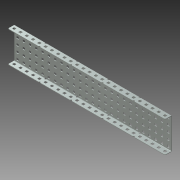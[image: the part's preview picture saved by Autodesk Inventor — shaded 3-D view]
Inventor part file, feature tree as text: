
AUTODESK INVENTOR PART (.ipt)
format: ipt  version: 2015 (Build 190159000, 159)  size: 3,633,664 bytes
history: native  units: mm (DEFAULTED — no unit token found)
features: other x175, extrude x175, pattern_linear x2, sketch x2, imported_body x1, plane x1, mirror x1
ambient origin geometry x8: Origin, YZ Plane, XZ Plane, XY Plane, X Axis, Y Axis, Z Axis, Center Point
bodies: Solid1 (feature_tree)
feature tree (357):
  imported_body  "Base1"
  pattern_linear  "Rectangular Pattern1"  Count1=25  [1 undecoded]
  pattern_linear  "Rectangular Pattern2"  Spacing1=12.7mm  [1 undecoded]
  plane  "Work Plane1"
  mirror  "Mirror1"
  sketch  "Sketch1"  dims[d1=1.1684mm]
  other  "Srf1"
  other  "Srf2"
  other  "Srf3"
  other  "Srf4"
  other  "Srf5"
  other  "Srf6"
  other  "Srf7"
  other  "Srf8"
  other  "Srf9"
  other  "Srf10"
  other  "Srf11"
  other  "Srf12"
  other  "Srf13"
  other  "Srf14"
  other  "Srf15"
  other  "Srf16"
  other  "Srf17"
  other  "Srf18"
  other  "Srf19"
  other  "Srf20"
  other  "Srf21"
  other  "Srf22"
  other  "Srf23"
  other  "Srf24"
  other  "Srf25"
  other  "Srf26"
  other  "Srf27"
  other  "Srf28"
  other  "Srf29"
  other  "Srf30"
  other  "Srf31"
  other  "Srf32"
  other  "Srf33"
  other  "Srf34"
  other  "Srf35"
  other  "Srf36"
  other  "Srf37"
  other  "Srf38"
  other  "Srf39"
  other  "Srf40"
  other  "Srf41"
  other  "Srf42"
  other  "Srf43"
  other  "Srf44"
  other  "Srf45"
  other  "Srf46"
  other  "Srf47"
  other  "Srf48"
  other  "Srf49"
  other  "Srf50"
  other  "Srf51"
  other  "Srf52"
  other  "Srf53"
  other  "Srf54"
  other  "Srf55"
  other  "Srf56"
  other  "Srf57"
  other  "Srf58"
  other  "Srf59"
  other  "Srf60"
  other  "Srf61"
  other  "Srf62"
  other  "Srf63"
  other  "Srf64"
  other  "Srf65"
  other  "Srf66"
  other  "Srf67"
  other  "Srf68"
  other  "Srf69"
  other  "Srf70"
  other  "Srf71"
  other  "Srf72"
  other  "Srf73"
  other  "Srf74"
  other  "Srf75"
  other  "Srf76"
  other  "Srf77"
  other  "Srf78"
  other  "Srf79"
  other  "Srf80"
  other  "Srf81"
  other  "Srf82"
  other  "Srf83"
  other  "Srf84"
  other  "Srf85"
  other  "Srf86"
  other  "Srf87"
  other  "Srf88"
  other  "Srf89"
  other  "Srf90"
  other  "Srf91"
  other  "Srf92"
  other  "Srf93"
  other  "Srf94"
  other  "Srf95"
  other  "Srf96"
  other  "Srf97"
  other  "Srf98"
  other  "Srf99"
  other  "Srf100"
  other  "Srf101"
  other  "Srf102"
  other  "Srf103"
  other  "Srf104"
  other  "Srf105"
  other  "Srf106"
  other  "Srf107"
  other  "Srf108"
  other  "Srf109"
  other  "Srf110"
  other  "Srf111"
  other  "Srf112"
  other  "Srf113"
  other  "Srf114"
  other  "Srf115"
  other  "Srf116"
  other  "Srf117"
  other  "Srf118"
  other  "Srf119"
  other  "Srf120"
  other  "Srf121"
  other  "Srf122"
  other  "Srf123"
  other  "Srf124"
  other  "Srf125"
  sketch  "Sketch2"  dims[d2=0.0mm d3=250.0mm d5=12.7mm d6=50.0mm d8=12.7mm d9=1.1684mm d10=0.0mm d11=250.0mm d13=12.7mm d14=0.0mm d15=0.0mm d16=0.0mm d17=0.0mm d18=0.0mm d19=0.0mm d20=0.0mm d21=0.0mm d22=0.0mm d23=0.0mm d24=0.0mm d25=0.0mm d26=0.0mm d27=0.0mm d28=0.0mm d29=0.0mm d30=0.0mm d31=0.0mm d32=0.0mm d33=0.0mm d34=0.0mm d35=0.0mm d36=0.0mm d37=0.0mm d38=0.0mm d39=0.0mm d40=0.0mm d41=0.0mm d42=0.0mm d43=0.0mm d44=0.0mm d45=0.0mm d46=0.0mm d47=0.0mm d48=0.0mm d49=0.0mm d50=0.0mm d51=0.0mm d52=0.0mm d53=0.0mm d54=0.0mm d55=0.0mm d56=0.0mm d57=0.0mm d58=0.0mm d59=0.0mm d60=0.0mm d61=0.0mm d62=0.0mm d63=0.0mm d64=0.0mm d65=0.0mm d66=0.0mm d67=0.0mm d68=0.0mm d69=0.0mm d70=0.0mm d71=0.0mm d72=0.0mm d73=0.0mm d74=0.0mm d75=0.0mm d76=0.0mm d77=0.0mm d78=0.0mm d79=0.0mm d80=0.0mm d81=0.0mm d82=0.0mm d83=0.0mm d84=0.0mm d85=0.0mm d86=0.0mm d87=0.0mm d88=0.0mm d89=0.0mm d90=0.0mm d91=0.0mm d92=0.0mm d93=0.0mm d94=0.0mm d95=0.0mm d96=0.0mm d97=0.0mm d98=0.0mm d99=0.0mm d100=0.0mm d101=0.0mm d102=0.0mm d103=0.0mm d104=0.0mm d105=0.0mm d106=0.0mm d107=0.0mm d108=0.0mm d109=0.0mm d110=0.0mm d111=0.0mm d112=0.0mm d113=0.0mm d114=0.0mm d115=0.0mm d116=0.0mm d117=0.0mm d118=0.0mm d119=0.0mm d120=0.0mm d121=0.0mm d122=0.0mm d123=0.0mm d124=0.0mm d125=0.0mm d126=0.0mm d127=0.0mm d128=0.0mm d129=0.0mm d130=0.0mm d131=0.0mm d132=0.0mm d133=0.0mm d134=0.0mm d135=0.0mm d136=0.0mm d137=0.0mm d138=0.0mm d139=0.0mm d140=0.0mm d141=0.0mm d142=0.0mm d143=0.0mm d144=0.0mm d145=0.0mm d146=0.0mm d147=0.0mm d148=0.0mm d149=0.0mm d150=0.0mm d151=0.0mm d152=0.0mm d153=0.0mm d154=0.0mm d155=0.0mm d156=0.0mm d157=0.0mm d158=0.0mm d159=0.0mm d160=0.0mm d161=0.0mm d162=0.0mm d163=0.0mm d164=0.0mm d165=0.0mm d166=0.0mm d167=0.0mm d168=0.0mm d169=0.0mm d170=0.0mm d171=0.0mm d172=0.0mm d173=0.0mm d174=0.0mm d175=0.0mm d176=0.0mm d177=0.0mm d178=0.0mm d179=0.0mm d180=0.0mm d181=0.0mm d182=0.0mm d183=0.0mm d184=0.0mm d185=0.0mm d186=0.0mm d187=0.0mm d188=0.0mm d189=0.0mm d190=0.0mm d191=0.0mm d192=0.0mm d193=0.0mm d194=0.0mm d195=0.0mm d196=0.0mm d197=0.0mm d198=0.0mm d199=0.0mm d200=0.0mm d201=0.0mm d202=0.0mm d203=0.0mm d204=0.0mm d205=0.0mm d206=0.0mm d207=0.0mm d208=0.0mm d209=0.0mm d210=0.0mm d211=0.0mm d212=0.0mm d213=0.0mm d214=0.0mm d215=0.0mm d216=0.0mm d217=0.0mm d218=0.0mm d219=0.0mm d220=0.0mm d221=0.0mm d222=0.0mm d223=0.0mm d224=0.0mm d225=0.0mm d226=0.0mm d227=0.0mm d228=0.0mm d229=0.0mm d230=0.0mm d231=0.0mm d232=0.0mm d233=0.0mm d234=0.0mm d235=0.0mm d236=0.0mm d237=0.0mm d238=0.0mm d239=0.0mm d240=0.0mm d241=0.0mm d242=0.0mm d243=0.0mm d244=0.0mm d245=0.0mm d246=0.0mm d247=0.0mm d248=0.0mm d249=0.0mm d250=0.0mm d251=0.0mm d252=0.0mm d253=0.0mm d254=0.0mm d255=0.0mm d256=0.0mm d257=0.0mm d258=0.0mm d259=0.0mm d260=0.0mm d261=0.0mm d262=0.0mm d263=0.0mm d264=0.0mm d265=0.0mm d266=0.0mm d267=0.0mm d268=0.0mm d269=0.0mm d270=0.0mm d271=0.0mm d272=0.0mm d273=0.0mm d274=0.0mm d275=0.0mm d276=0.0mm d277=0.0mm d278=0.0mm d279=0.0mm d280=0.0mm d281=0.0mm d282=0.0mm d283=0.0mm d284=0.0mm d285=0.0mm d286=0.0mm d287=0.0mm d288=0.0mm d289=0.0mm d290=0.0mm d291=0.0mm d292=0.0mm d293=0.0mm d294=0.0mm d295=0.0mm d296=0.0mm d297=0.0mm d298=0.0mm d299=0.0mm d300=0.0mm d301=0.0mm d302=0.0mm d303=0.0mm d304=0.0mm d305=0.0mm d306=0.0mm d307=0.0mm d308=0.0mm d309=0.0mm d310=0.0mm d311=0.0mm d312=0.0mm d313=0.0mm d314=0.0mm d315=0.0mm d316=0.0mm d317=0.0mm d318=0.0mm d319=0.0mm d320=0.0mm d321=0.0mm d322=0.0mm d323=0.0mm d324=0.0mm d325=0.0mm d326=0.0mm d327=0.0mm d328=0.0mm d329=0.0mm d330=0.0mm d331=0.0mm d332=0.0mm d333=0.0mm d334=0.0mm d335=0.0mm d336=0.0mm d337=0.0mm d338=0.0mm d339=0.0mm d340=0.0mm d341=0.0mm d342=0.0mm d343=0.0mm d344=0.0mm d345=0.0mm d346=0.0mm d347=0.0mm d348=0.0mm d349=0.0mm d350=0.0mm d351=0.0mm d352=0.0mm d353=0.0mm d354=0.0mm d355=0.0mm d356=0.0mm d357=0.0mm d358=0.0mm d359=0.0mm d360=0.0mm d361=0.0mm d362=0.0mm d363=0.0mm]
  other  "Srf126"
  other  "Srf127"
  other  "Srf128"
  other  "Srf129"
  other  "Srf130"
  other  "Srf131"
  other  "Srf132"
  other  "Srf133"
  other  "Srf134"
  other  "Srf135"
  other  "Srf136"
  other  "Srf137"
  other  "Srf138"
  other  "Srf139"
  other  "Srf140"
  other  "Srf141"
  other  "Srf142"
  other  "Srf143"
  other  "Srf144"
  other  "Srf145"
  other  "Srf146"
  other  "Srf147"
  other  "Srf148"
  other  "Srf149"
  other  "Srf150"
  other  "Srf175"
  other  "Srf151"
  other  "Srf152"
  other  "Srf153"
  other  "Srf154"
  other  "Srf155"
  other  "Srf156"
  other  "Srf157"
  other  "Srf158"
  other  "Srf159"
  other  "Srf160"
  other  "Srf161"
  other  "Srf162"
  other  "Srf163"
  other  "Srf164"
  other  "Srf165"
  other  "Srf166"
  other  "Srf167"
  other  "Srf168"
  other  "Srf169"
  other  "Srf170"
  other  "Srf171"
  other  "Srf172"
  other  "Srf173"
  other  "Srf174"
  extrude  "ExtrusionSrf1"  Depth=50.0mm
  extrude  "ExtrusionSrf126"  Depth=1.1684mm
  extrude  "ExtrusionSrf2"  TaperAngle=0.0deg  [1 undecoded]
  extrude  "ExtrusionSrf3"  Depth=250.0mm
  extrude  "ExtrusionSrf4"  Depth=12.7mm
  extrude  "ExtrusionSrf5"  TaperAngle=0.0deg  [1 undecoded]
  extrude  "ExtrusionSrf6"  TaperAngle=0.0deg  [1 undecoded]
  extrude  "ExtrusionSrf7"  TaperAngle=0.0deg  [1 undecoded]
  extrude  "ExtrusionSrf8"  TaperAngle=0.0deg  [1 undecoded]
  extrude  "ExtrusionSrf9"  TaperAngle=0.0deg  [1 undecoded]
  extrude  "ExtrusionSrf10"  TaperAngle=0.0deg  [1 undecoded]
  extrude  "ExtrusionSrf11"  TaperAngle=0.0deg  [1 undecoded]
  extrude  "ExtrusionSrf12"  TaperAngle=0.0deg  [1 undecoded]
  extrude  "ExtrusionSrf13"  TaperAngle=0.0deg  [1 undecoded]
  extrude  "ExtrusionSrf14"  TaperAngle=0.0deg  [1 undecoded]
  extrude  "ExtrusionSrf15"  TaperAngle=0.0deg  [1 undecoded]
  extrude  "ExtrusionSrf16"  TaperAngle=0.0deg  [1 undecoded]
  extrude  "ExtrusionSrf17"  TaperAngle=0.0deg  [1 undecoded]
  extrude  "ExtrusionSrf18"  TaperAngle=0.0deg  [1 undecoded]
  extrude  "ExtrusionSrf19"  TaperAngle=0.0deg  [1 undecoded]
  extrude  "ExtrusionSrf20"  TaperAngle=0.0deg  [1 undecoded]
  extrude  "ExtrusionSrf21"  TaperAngle=0.0deg  [1 undecoded]
  extrude  "ExtrusionSrf22"  TaperAngle=0.0deg  [1 undecoded]
  extrude  "ExtrusionSrf23"  TaperAngle=0.0deg  [1 undecoded]
  extrude  "ExtrusionSrf24"  TaperAngle=0.0deg  [1 undecoded]
  extrude  "ExtrusionSrf25"  TaperAngle=0.0deg  [1 undecoded]
  extrude  "ExtrusionSrf26"  TaperAngle=0.0deg  [1 undecoded]
  extrude  "ExtrusionSrf27"  TaperAngle=0.0deg  [1 undecoded]
  extrude  "ExtrusionSrf28"  TaperAngle=0.0deg  [1 undecoded]
  extrude  "ExtrusionSrf29"  TaperAngle=0.0deg  [1 undecoded]
  extrude  "ExtrusionSrf30"  TaperAngle=0.0deg  [1 undecoded]
  extrude  "ExtrusionSrf31"  TaperAngle=0.0deg  [1 undecoded]
  extrude  "ExtrusionSrf32"  TaperAngle=0.0deg  [1 undecoded]
  extrude  "ExtrusionSrf33"  TaperAngle=0.0deg  [1 undecoded]
  extrude  "ExtrusionSrf34"  TaperAngle=0.0deg  [1 undecoded]
  extrude  "ExtrusionSrf35"  TaperAngle=0.0deg  [1 undecoded]
  extrude  "ExtrusionSrf36"  TaperAngle=0.0deg  [1 undecoded]
  extrude  "ExtrusionSrf37"  TaperAngle=0.0deg  [1 undecoded]
  extrude  "ExtrusionSrf38"  TaperAngle=0.0deg  [1 undecoded]
  extrude  "ExtrusionSrf39"  TaperAngle=0.0deg  [1 undecoded]
  extrude  "ExtrusionSrf40"  TaperAngle=0.0deg  [1 undecoded]
  extrude  "ExtrusionSrf41"  TaperAngle=0.0deg  [1 undecoded]
  extrude  "ExtrusionSrf42"  TaperAngle=0.0deg  [1 undecoded]
  extrude  "ExtrusionSrf43"  TaperAngle=0.0deg  [1 undecoded]
  extrude  "ExtrusionSrf44"  TaperAngle=0.0deg  [1 undecoded]
  extrude  "ExtrusionSrf45"  TaperAngle=0.0deg  [1 undecoded]
  extrude  "ExtrusionSrf46"  TaperAngle=0.0deg  [1 undecoded]
  extrude  "ExtrusionSrf47"  TaperAngle=0.0deg  [1 undecoded]
  extrude  "ExtrusionSrf48"  TaperAngle=0.0deg  [1 undecoded]
  extrude  "ExtrusionSrf49"  TaperAngle=0.0deg  [1 undecoded]
  extrude  "ExtrusionSrf50"  TaperAngle=0.0deg  [1 undecoded]
  extrude  "ExtrusionSrf51"  TaperAngle=0.0deg  [1 undecoded]
  extrude  "ExtrusionSrf52"  TaperAngle=0.0deg  [1 undecoded]
  extrude  "ExtrusionSrf53"  TaperAngle=0.0deg  [1 undecoded]
  extrude  "ExtrusionSrf54"  TaperAngle=0.0deg  [1 undecoded]
  extrude  "ExtrusionSrf55"  TaperAngle=0.0deg  [1 undecoded]
  extrude  "ExtrusionSrf56"  TaperAngle=0.0deg  [1 undecoded]
  extrude  "ExtrusionSrf57"  TaperAngle=0.0deg  [1 undecoded]
  extrude  "ExtrusionSrf58"  TaperAngle=0.0deg  [1 undecoded]
  extrude  "ExtrusionSrf59"  TaperAngle=0.0deg  [1 undecoded]
  extrude  "ExtrusionSrf60"  TaperAngle=0.0deg  [1 undecoded]
  extrude  "ExtrusionSrf61"  TaperAngle=0.0deg  [1 undecoded]
  extrude  "ExtrusionSrf62"  TaperAngle=0.0deg  [1 undecoded]
  extrude  "ExtrusionSrf63"  TaperAngle=0.0deg  [1 undecoded]
  extrude  "ExtrusionSrf64"  TaperAngle=0.0deg  [1 undecoded]
  extrude  "ExtrusionSrf65"  TaperAngle=0.0deg  [1 undecoded]
  extrude  "ExtrusionSrf66"  TaperAngle=0.0deg  [1 undecoded]
  extrude  "ExtrusionSrf67"  TaperAngle=0.0deg  [1 undecoded]
  extrude  "ExtrusionSrf68"  TaperAngle=0.0deg  [1 undecoded]
  extrude  "ExtrusionSrf69"  TaperAngle=0.0deg  [1 undecoded]
  extrude  "ExtrusionSrf70"  TaperAngle=0.0deg  [1 undecoded]
  extrude  "ExtrusionSrf71"  TaperAngle=0.0deg  [1 undecoded]
  extrude  "ExtrusionSrf72"  TaperAngle=0.0deg  [1 undecoded]
  extrude  "ExtrusionSrf73"  TaperAngle=0.0deg  [1 undecoded]
  extrude  "ExtrusionSrf74"  TaperAngle=0.0deg  [1 undecoded]
  extrude  "ExtrusionSrf75"  TaperAngle=0.0deg  [1 undecoded]
  extrude  "ExtrusionSrf76"  TaperAngle=0.0deg  [1 undecoded]
  extrude  "ExtrusionSrf77"  TaperAngle=0.0deg  [1 undecoded]
  extrude  "ExtrusionSrf78"  TaperAngle=0.0deg  [1 undecoded]
  extrude  "ExtrusionSrf79"  TaperAngle=0.0deg  [1 undecoded]
  extrude  "ExtrusionSrf80"  TaperAngle=0.0deg  [1 undecoded]
  extrude  "ExtrusionSrf81"  TaperAngle=0.0deg  [1 undecoded]
  extrude  "ExtrusionSrf82"  TaperAngle=0.0deg  [1 undecoded]
  extrude  "ExtrusionSrf83"  TaperAngle=0.0deg  [1 undecoded]
  extrude  "ExtrusionSrf84"  TaperAngle=0.0deg  [1 undecoded]
  extrude  "ExtrusionSrf85"  TaperAngle=0.0deg  [1 undecoded]
  extrude  "ExtrusionSrf86"  TaperAngle=0.0deg  [1 undecoded]
  extrude  "ExtrusionSrf87"  TaperAngle=0.0deg  [1 undecoded]
  extrude  "ExtrusionSrf88"  TaperAngle=0.0deg  [1 undecoded]
  extrude  "ExtrusionSrf89"  TaperAngle=0.0deg  [1 undecoded]
  extrude  "ExtrusionSrf90"  TaperAngle=0.0deg  [1 undecoded]
  extrude  "ExtrusionSrf91"  TaperAngle=0.0deg  [1 undecoded]
  extrude  "ExtrusionSrf92"  TaperAngle=0.0deg  [1 undecoded]
  extrude  "ExtrusionSrf93"  TaperAngle=0.0deg  [1 undecoded]
  extrude  "ExtrusionSrf94"  TaperAngle=0.0deg  [1 undecoded]
  extrude  "ExtrusionSrf95"  TaperAngle=0.0deg  [1 undecoded]
  extrude  "ExtrusionSrf96"  TaperAngle=0.0deg  [1 undecoded]
  extrude  "ExtrusionSrf97"  TaperAngle=0.0deg  [1 undecoded]
  extrude  "ExtrusionSrf98"  TaperAngle=0.0deg  [1 undecoded]
  extrude  "ExtrusionSrf99"  TaperAngle=0.0deg  [1 undecoded]
  extrude  "ExtrusionSrf100"  TaperAngle=0.0deg  [1 undecoded]
  extrude  "ExtrusionSrf101"  TaperAngle=0.0deg  [1 undecoded]
  extrude  "ExtrusionSrf102"  TaperAngle=0.0deg  [1 undecoded]
  extrude  "ExtrusionSrf103"  TaperAngle=0.0deg  [1 undecoded]
  extrude  "ExtrusionSrf104"  TaperAngle=0.0deg  [1 undecoded]
  extrude  "ExtrusionSrf105"  TaperAngle=0.0deg  [1 undecoded]
  extrude  "ExtrusionSrf106"  TaperAngle=0.0deg  [1 undecoded]
  extrude  "ExtrusionSrf107"  TaperAngle=0.0deg  [1 undecoded]
  extrude  "ExtrusionSrf108"  TaperAngle=0.0deg  [1 undecoded]
  extrude  "ExtrusionSrf109"  TaperAngle=0.0deg  [1 undecoded]
  extrude  "ExtrusionSrf110"  TaperAngle=0.0deg  [1 undecoded]
  extrude  "ExtrusionSrf111"  TaperAngle=0.0deg  [1 undecoded]
  extrude  "ExtrusionSrf112"  TaperAngle=0.0deg  [1 undecoded]
  extrude  "ExtrusionSrf113"  TaperAngle=0.0deg  [1 undecoded]
  extrude  "ExtrusionSrf114"  TaperAngle=0.0deg  [1 undecoded]
  extrude  "ExtrusionSrf115"  TaperAngle=0.0deg  [1 undecoded]
  extrude  "ExtrusionSrf116"  TaperAngle=0.0deg  [1 undecoded]
  extrude  "ExtrusionSrf117"  TaperAngle=0.0deg  [1 undecoded]
  extrude  "ExtrusionSrf118"  TaperAngle=0.0deg  [1 undecoded]
  extrude  "ExtrusionSrf119"  TaperAngle=0.0deg  [1 undecoded]
  extrude  "ExtrusionSrf120"  TaperAngle=0.0deg  [1 undecoded]
  extrude  "ExtrusionSrf121"  TaperAngle=0.0deg  [1 undecoded]
  extrude  "ExtrusionSrf122"  TaperAngle=0.0deg  [1 undecoded]
  extrude  "ExtrusionSrf123"  TaperAngle=0.0deg  [1 undecoded]
  extrude  "ExtrusionSrf124"  TaperAngle=0.0deg  [1 undecoded]
  extrude  "ExtrusionSrf125"  TaperAngle=0.0deg  [1 undecoded]
  extrude  "ExtrusionSrf127"  TaperAngle=0.0deg  [1 undecoded]
  extrude  "ExtrusionSrf128"  TaperAngle=0.0deg  [1 undecoded]
  extrude  "ExtrusionSrf129"  TaperAngle=0.0deg  [1 undecoded]
  extrude  "ExtrusionSrf130"  TaperAngle=0.0deg  [1 undecoded]
  extrude  "ExtrusionSrf131"  TaperAngle=0.0deg  [1 undecoded]
  extrude  "ExtrusionSrf132"  TaperAngle=0.0deg  [1 undecoded]
  extrude  "ExtrusionSrf133"  TaperAngle=0.0deg  [1 undecoded]
  extrude  "ExtrusionSrf134"  TaperAngle=0.0deg  [1 undecoded]
  extrude  "ExtrusionSrf135"  TaperAngle=0.0deg  [1 undecoded]
  extrude  "ExtrusionSrf136"  TaperAngle=0.0deg  [1 undecoded]
  extrude  "ExtrusionSrf137"  TaperAngle=0.0deg  [1 undecoded]
  extrude  "ExtrusionSrf138"  TaperAngle=0.0deg  [1 undecoded]
  extrude  "ExtrusionSrf139"  TaperAngle=0.0deg  [1 undecoded]
  extrude  "ExtrusionSrf140"  TaperAngle=0.0deg  [1 undecoded]
  extrude  "ExtrusionSrf141"  TaperAngle=0.0deg  [1 undecoded]
  extrude  "ExtrusionSrf142"  TaperAngle=0.0deg  [1 undecoded]
  extrude  "ExtrusionSrf143"  TaperAngle=0.0deg  [1 undecoded]
  extrude  "ExtrusionSrf144"  TaperAngle=0.0deg  [1 undecoded]
  extrude  "ExtrusionSrf145"  TaperAngle=0.0deg  [1 undecoded]
  extrude  "ExtrusionSrf146"  TaperAngle=0.0deg  [1 undecoded]
  extrude  "ExtrusionSrf147"  TaperAngle=0.0deg  [1 undecoded]
  extrude  "ExtrusionSrf148"  TaperAngle=0.0deg  [1 undecoded]
  extrude  "ExtrusionSrf149"  TaperAngle=0.0deg  [1 undecoded]
  extrude  "ExtrusionSrf150"  TaperAngle=0.0deg  [1 undecoded]
  extrude  "ExtrusionSrf151"  TaperAngle=0.0deg  [1 undecoded]
  extrude  "ExtrusionSrf152"  TaperAngle=0.0deg  [1 undecoded]
  extrude  "ExtrusionSrf153"  TaperAngle=0.0deg  [1 undecoded]
  extrude  "ExtrusionSrf154"  TaperAngle=0.0deg  [1 undecoded]
  extrude  "ExtrusionSrf155"  TaperAngle=0.0deg  [1 undecoded]
  extrude  "ExtrusionSrf156"  TaperAngle=0.0deg  [1 undecoded]
  extrude  "ExtrusionSrf157"  TaperAngle=0.0deg  [1 undecoded]
  extrude  "ExtrusionSrf158"  TaperAngle=0.0deg  [1 undecoded]
  extrude  "ExtrusionSrf159"  TaperAngle=0.0deg  [1 undecoded]
  extrude  "ExtrusionSrf160"  TaperAngle=0.0deg  [1 undecoded]
  extrude  "ExtrusionSrf161"  TaperAngle=0.0deg  [1 undecoded]
  extrude  "ExtrusionSrf162"  TaperAngle=0.0deg  [1 undecoded]
  extrude  "ExtrusionSrf163"  TaperAngle=0.0deg  [1 undecoded]
  extrude  "ExtrusionSrf164"  TaperAngle=0.0deg  [1 undecoded]
  extrude  "ExtrusionSrf165"  TaperAngle=0.0deg  [1 undecoded]
  extrude  "ExtrusionSrf166"  TaperAngle=0.0deg  [1 undecoded]
  extrude  "ExtrusionSrf167"  TaperAngle=0.0deg  [1 undecoded]
  extrude  "ExtrusionSrf168"  TaperAngle=0.0deg  [1 undecoded]
  extrude  "ExtrusionSrf169"  TaperAngle=0.0deg  [1 undecoded]
  extrude  "ExtrusionSrf170"  TaperAngle=0.0deg  [1 undecoded]
  extrude  "ExtrusionSrf171"  TaperAngle=0.0deg  [1 undecoded]
  extrude  "ExtrusionSrf172"  TaperAngle=0.0deg  [1 undecoded]
  extrude  "ExtrusionSrf173"  TaperAngle=0.0deg  [1 undecoded]
  extrude  "ExtrusionSrf174"  TaperAngle=0.0deg  [1 undecoded]
  extrude  "ExtrusionSrf175"  TaperAngle=0.0deg  [1 undecoded]
note: 173 required parameter values undecoded (feature->parameter linkage not recoverable at this tier; creation-order binding heuristic only, values carry confidence <= 0.55)
